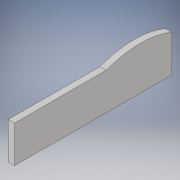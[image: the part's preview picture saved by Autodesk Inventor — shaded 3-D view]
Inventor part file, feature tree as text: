
AUTODESK INVENTOR PART (.ipt)
format: ipt  version: 2018 (Build 220112000, 112)  size: 94,208 bytes
history: native  units: in
note: dims shown in document units (in); Inventor stores cm internally (conversion verified against a paired STEP export)
features: extrude x1, sketch x1
ambient origin geometry x8: Origin, YZ Plane, XZ Plane, XY Plane, X Axis, Y Axis, Z Axis, Center Point
bodies: Solid1 (feature_tree)
feature tree (2):
  extrude  "Extrusion1"  Depth=5.8661in
  sketch  "Sketch1"  dims[d0=1.378in d1=5.8661in d2=0.2362in d3=0.0in]
